# Revit family: PRD_FrankeWS_WCPans_CAMPUS_CMPX597,CMPX597B,CMPX597G,CMPX597S,CMPX597W
name_source: partatom
category: Plumbing Fixtures
revit_build: Autodesk Revit 2018 (Build: 20190510_1515(x64)
units: mm (PartAtom-declared; Revit-internal decimal feet)

## family parameters
Cut with Voids When Loaded = No
Host = Face
OmniClass Number = 23.45.05.21.11
OmniClass Title = Water Closets
Part Type = Normal
Room Calculation Point = No
Round Connector Dimension = Use Diameter
Shared = No

## types (5) — shared parameters
AssetType = Fixed
Category = Pr_40_20_93_94, WC pans
Default Elevation = 500 mm  [stored 1.64042 ft]
DurationUnit = year
Finish = Satin finished
Form = WALL-HUNG
IfcExportAs = IfcSanitaryTerminalType
IfcExportType = TOILETPAN
InletSize = 55  [stored 0.180446 ft]
IntegralAccessories = Includes Mounting material
Manufacturer = KWC Group AG
ManufacturerName = KWC Group AG
ManufacturerURL = www.kwc.com
MaterialsBody = Stainless steel
MaterialsFinishAndColour = Stainless steel
MinimumFlushingCapacity = 4.00 L
NBSDescription = WC pans
NBSReference = 45-35-70/384
NominalLength = 500 mm  [stored 1.64042 ft]
NominalWidth = 360 mm  [stored 1.1811 ft]
PanColor = Stainless steel
PanMaterial = Stainless steel
PanMounting = WallHung
ProductInformation = https://pim.kwc.com
SeatPadsMaterial = PRD_AR_SyntheticGrey
SpilloverLevel = 400 mm  [stored 1.31234 ft]
ToiletPanType = Other
ToiletType = LooseCoupled
URL = www.kwc.com
Uniclass2015Code = Pr_40_20_93_94
Uniclass2015Title = WC pans
Uniclass2015Version = Products v1.7
Version = 1
WC Material = PRD_AR_StainlessSteel_SatinFinished
WarrantyDurationUnit = year
WasteSize = 100  [stored 0.328084 ft]

## per-type parameters (varying)
| type | BIMObjectName | Description | Features | GrossWeight | ModelNumber | Name | NetWeight | NominalDepth | NominalHeight | SeatPads | Size | Visible | WCseatMaterial |
| CMPX597 | PRD_AR_WCPans_CAMPUS_CMPX597 | Floor standing WC pan with shroud to the floor, stainless steel, surface satin finished, material thickness 1.6 mm, flushing certificated to EN 997, concealed flushing rim with min. 4 liter flushing capacity, with a shrouded 100 mm diameter horizontal 'P' trap outlet, pressed seat area tapered towards centre, all edges curved, fixing with mounting plate supplied, conform to EN 33, includes security screws. 4 litre flush EN 997 approved. Without seat. | stainless steel, 1.60 mm, satin finished, wall and floor mounting, 360x400x500 mm (WxHxD) | 16.66 kg | 2000100153 | CAMPUS WC CMPX597 | 15.76 kg | 400 mm  [stored 1.31234 ft] | 400 mm  [stored 1.31234 ft] | No | 360 x 400 x 500 mm | No | <By Category> |
| CMPX597S | PRD_AR_WCPans_CAMPUS_CMPX597S | Floor standing WC pan with shroud to the floor, stainless steel, surface satin finished, material thickness 1.6 mm, flushing certificated to EN 997, concealed flushing rim with min. 4 liter flushing capacity, with a shrouded 100 mm diameter horizontal 'P' trap outlet, pressed seat area tapered towards centre, all edges curved, fixing with mounting plate supplied, conform to EN 33, includes security screws. 4 litre flush EN 997 approved. With seat pads. | stainless steel, 1.60 mm, satin finished, wall and floor mounting, 360x412x500 mm (WxHxD) | 17.34 kg | 2000100154 | CAMPUS WC CMPX597S | 16.54 kg | 412 mm  [stored 1.35171 ft] | 412 mm  [stored 1.35171 ft] | Yes | 360 x 412 x 500 mm | No | <By Category> |
| CMPX597B | PRD_AR_WCPans_CAMPUS_CMPX597B | Floor standing WC pan with shroud to the floor, stainless steel, surface satin finished, material thickness 1.6 mm, flushing certificated to EN 997, concealed flushing rim with min. 4 liter flushing capacity, with a shrouded 100 mm diameter horizontal 'P' trap outlet, pressed seat area tapered towards centre, all edges curved, fixing with mounting plate supplied, conform to EN 33, includes security screws. 4 litre flush EN 997 approved. With black WC seat. | stainless steel, 1.60 mm, satin finished, wall and floor mounting, 360x456x500 mm (WxHxD) | 19.24 kg | 2000100156 | CAMPUS WC CMPX597B | 17.08 kg | 456 mm  [stored 1.49606 ft] | 456 mm  [stored 1.49606 ft] | No | 360 x 456 x 500 mm | Yes | PRD_AR_SyntheticBlack |
| CMPX597G | PRD_AR_WCPans_CAMPUS_CMPX597G | Floor standing WC pan with shroud to the floor, stainless steel, surface satin finished, material thickness 1.6 mm, flushing certificated to EN 997, concealed flushing rim with min. 4 liter flushing capacity, with a shrouded 100 mm diameter horizontal 'P' trap outlet, pressed seat area tapered towards centre, all edges curved, fixing with mounting plate supplied, conform to EN 33, includes security screws. 4 litre flush EN 997 approved. With grey WC seat. | stainless steel, 1.60 mm, satin finished, wall and floor mounting, 360x456x500 mm (WxHxD) | 19.24 kg | 2000100157 | CAMPUS WC CMPX597G | 17.08 kg | 456 mm  [stored 1.49606 ft] | 456 mm  [stored 1.49606 ft] | No | 360 x 456 x 500 mm | Yes | PRD_AR_SyntheticGrey |
| CMPX597W | PRD_AR_WCPans_CAMPUS_CMPX597W | Floor standing WC pan with shroud to the floor, stainless steel, surface satin finished, material thickness 1.6 mm, flushing certificated to EN 997, concealed flushing rim with min. 4 liter flushing capacity, with a shrouded 100 mm diameter horizontal 'P' trap outlet, pressed seat area tapered towards centre, all edges curved, fixing with mounting plate supplied, conform to EN 33, includes security screws. 4 litre flush EN 997 approved. With white WC seat. | stainless steel, 1.60 mm, satin finished, wall and floor mounting, 360x456x500 mm (WxHxD) | 19.24 kg | 2000100158 | CAMPUS WC CMPX597W | 17.08 kg | 456 mm  [stored 1.49606 ft] | 456 mm  [stored 1.49606 ft] | No | 360 x 456 x 500 mm | Yes | PRD_AR_SyntheticWhite |

note: column(s) folded — value = type name in every type: Model, ModelReference

note: [stored X ft] marks values corroborated as IEEE doubles in the binary element streams (Revit-internal decimal feet)

## geometry (parser evidence)
native form markers: Sweep x2
no freeform markers — native parametric forms only
